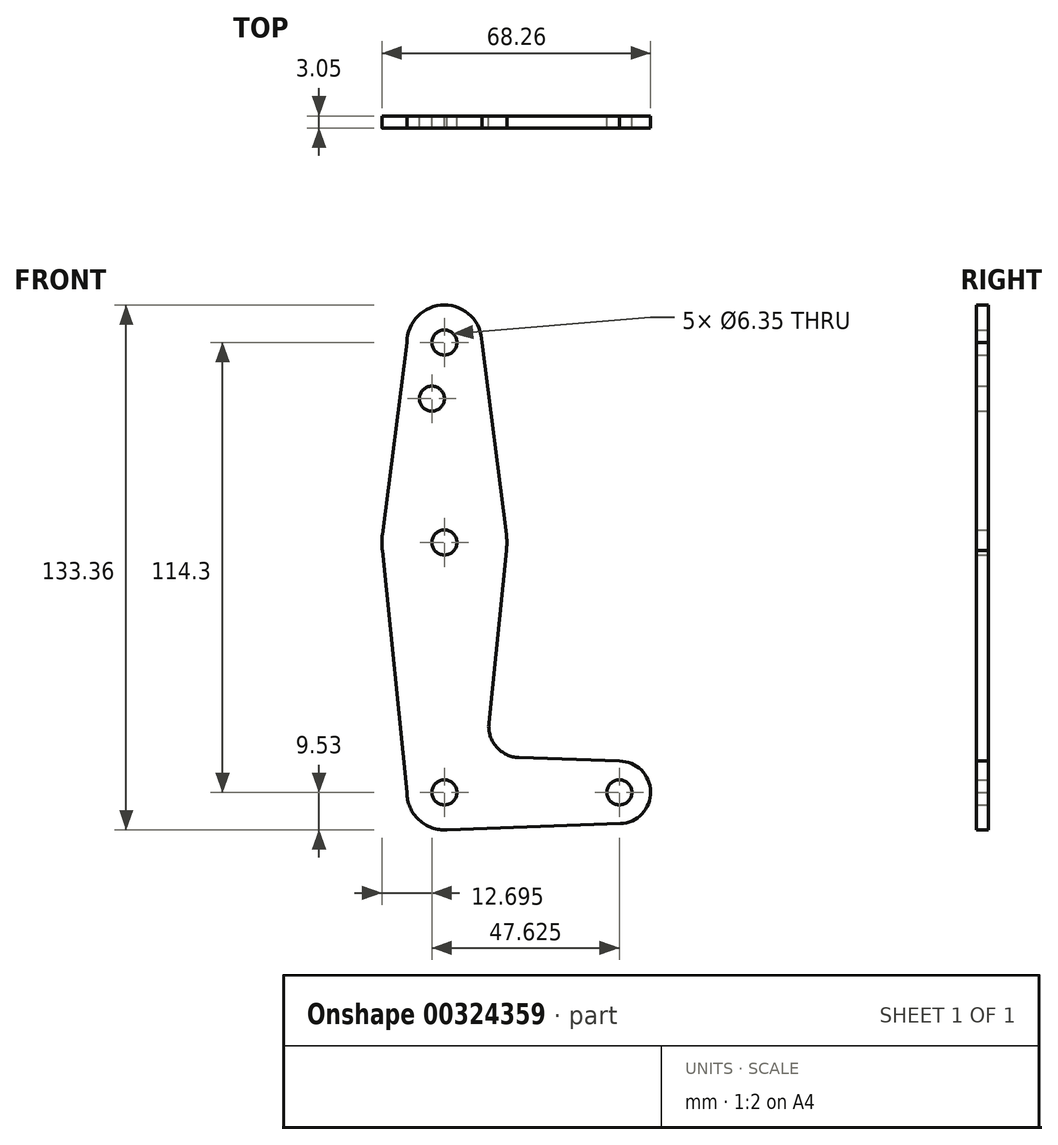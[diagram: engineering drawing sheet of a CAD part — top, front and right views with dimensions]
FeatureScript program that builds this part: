
annotation { "Feature Type Name" : "Feature", "Feature Type Description" : "" }
export const myFeature = defineFeature(function(context is Context, id is Id, definition is map)
    precondition{}
    {
        {
            var Q0;
            Q0=qCreatedBy(makeId("Front.planeOp"),FACE);
            var sketch = newSketch(context, id + "F0", { "sketchPlane" : qUnion([Q0])});
            skLineSegment(sketch, "E0", {"start": v(0, 0) * mm, "end": v(0, 114.3) * mm, "construction": true});
            skLineSegment(sketch, "E1", {"start": v(0, 0) * mm, "end": v(44.45, 0) * mm, "construction": true});
            skCircle(sketch, "E2", {"center": v(0, 0) * mm, "radius": 9.53 * mm});
            skCircle(sketch, "E3", {"center": v(44.45, 0) * mm, "radius": 7.94 * mm});
            skCircle(sketch, "E4", {"center": v(0, 63.5) * mm, "radius": 15.88 * mm});
            skCircle(sketch, "E5", {"center": v(0, 114.3) * mm, "radius": 9.53 * mm});
            skLineSegment(sketch, "E6", {"start": v(0, -9.53) * mm, "end": v(44.73, -7.93) * mm});
            skLineSegment(sketch, "E7", {"start": v(18.93, 8.85) * mm, "end": v(44.45, 7.94) * mm});
            skLineSegment(sketch, "E8", {"start": v(-9.52, 0) * mm, "end": v(-15.75, 61.5) * mm});
            skLineSegment(sketch, "E9", {"start": v(-15.75, 65.5) * mm, "end": v(-9.52, 114.3) * mm});
            skLineSegment(sketch, "E10", {"start": v(9.52, 114.3) * mm, "end": v(15.75, 65.5) * mm});
            skLineSegment(sketch, "E11", {"start": v(15.75, 61.5) * mm, "end": v(11.3, 17.6) * mm});
            skCircle(sketch, "E12", {"center": v(0, 114.3) * mm, "radius": 3.18 * mm});
            skCircle(sketch, "E13", {"center": v(0, 63.5) * mm, "radius": 3.18 * mm});
            skCircle(sketch, "E14", {"center": v(0, 0) * mm, "radius": 3.18 * mm});
            skCircle(sketch, "E15", {"center": v(44.45, 0) * mm, "radius": 3.18 * mm});
            skCircle(sketch, "E16", {"center": v(-3.17, 100.03) * mm, "radius": 3.18 * mm});
            skArc(sketch, "E17.filletArc", {"start": v(11.3, 17.6) * mm, "mid": v(13.22, 11.57) * mm, "end": v(18.93, 8.85) * mm});
            skSolve(sketch);
        }
        {
            var Q0;
            Q0 = qSketchRegion(id + "F0", true);
            extrude(context, id + "F1", {"entities" : qUnion([Q0]), "depth" : 3.05 * mm});
        }
    });
